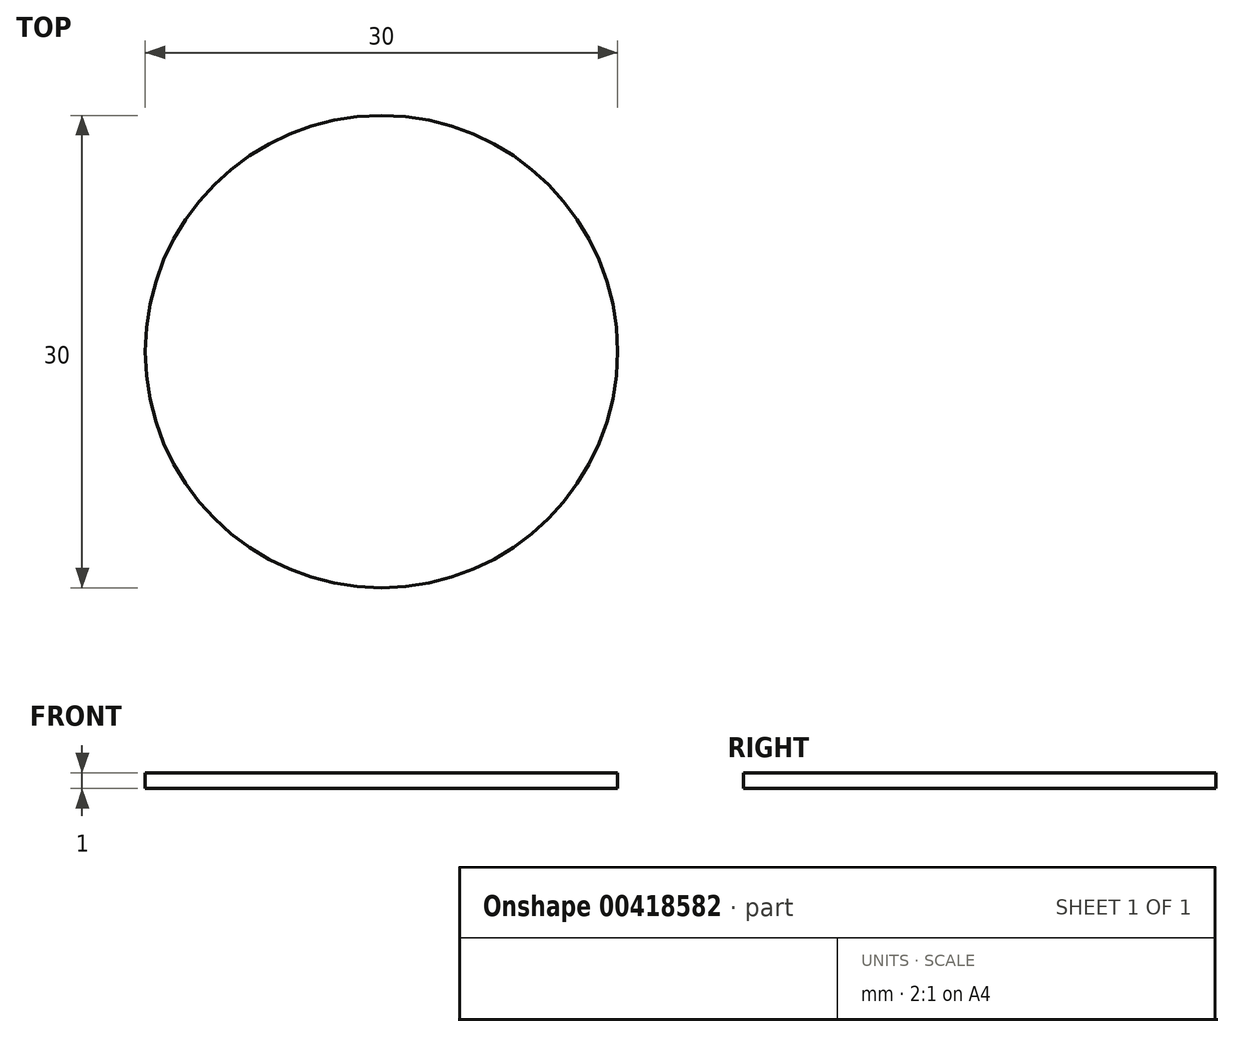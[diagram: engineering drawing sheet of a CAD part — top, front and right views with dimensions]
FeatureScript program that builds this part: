
annotation { "Feature Type Name" : "Feature", "Feature Type Description" : "" }
export const myFeature = defineFeature(function(context is Context, id is Id, definition is map)
    precondition{}
    {
        {
            var Q0;
            Q0=qCreatedBy(makeId("Top.planeOp"),FACE);
            var sketch = newSketch(context, id + "F0", { "sketchPlane" : qUnion([Q0])});
            skCircle(sketch, "E0", {"center": v(0, 0) * mm, "radius": 15 * mm});
            skSolve(sketch);
        }
        {
            var Q0;
            Q0 = qSketchRegion(id + "F0", true);
            extrude(context, id + "F1", {"entities" : qUnion([Q0]), "depth" : 1 * mm});
        }
    });
